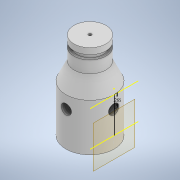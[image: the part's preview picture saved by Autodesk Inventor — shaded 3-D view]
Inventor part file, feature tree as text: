
AUTODESK INVENTOR PART (.ipt)
format: ipt  version: 2020 (Build 240168000, 168)  size: 215,040 bytes
history: native  units: in
note: dims shown in document units (in); Inventor stores cm internally (conversion verified against a paired STEP export)
features: sketch x5, hole x4, revolve x1, plane x1, extrude x1, pattern_circular x1
ambient origin geometry x8: Origin, YZ Plane, XZ Plane, XY Plane, X Axis, Y Axis, Z Axis, Center Point
bodies: Solid1 (feature_tree)
feature tree (13):
  revolve  "Revolution1"  [1 undecoded]
  hole  "Hole4"  [1 undecoded]
  sketch  "Sketch13"  dims[d4=0.095in d5=0.125in]
  plane  "Work Plane1"
  sketch  "Sketch14"  dims[d6=90.0deg d23=0.65in]
  hole  "Hole5"  [1 undecoded]
  hole  "Hole6"  [1 undecoded]
  extrude  "Extrusion3"  Depth=0.125in
  hole  "Hole8"  [1 undecoded]
  pattern_circular  "Circular Pattern5"  [2 undecoded]
  sketch  "Sketch1"  dims[d0=0.3328in d1=0.5in]
  sketch  "Sketch12"  dims[d2=90.0deg d3=0.057in]
  sketch  "Sketch16"  dims[d24=0.4466in d25=0.125in d54=0.3779in d72=0.3779in d83=0.5in d84=0.5in d85=0.0625in d86=0.75in d87=0.375in d88=0.25in d89=0.5635in d90=1.294in d91=0.8108in d92=0.2645in d93=0.0625in d94=0.75in d95=0.375in d96=0.25in d97=0.5635in d98=0.5in d99=0.8108in d100=0.211in d101=0.25in d102=0.375in d103=0.25in d104=0.5635in d105=0.25in d106=0.0in d119=0.25in d120=0.0in d121=0.196in d122=0.25in d123=0.375in d124=0.25in d125=0.5635in d126=0.25in d127=0.0in d137=0.3779in d155=0.3779in d173=0.3779in d191=0.3779in d211=1.5748in d212=360.0deg d221=0.3779in d239=0.3779in]
note: 7 required parameter values undecoded (feature->parameter linkage not recoverable at this tier; creation-order binding heuristic only, values carry confidence <= 0.55)